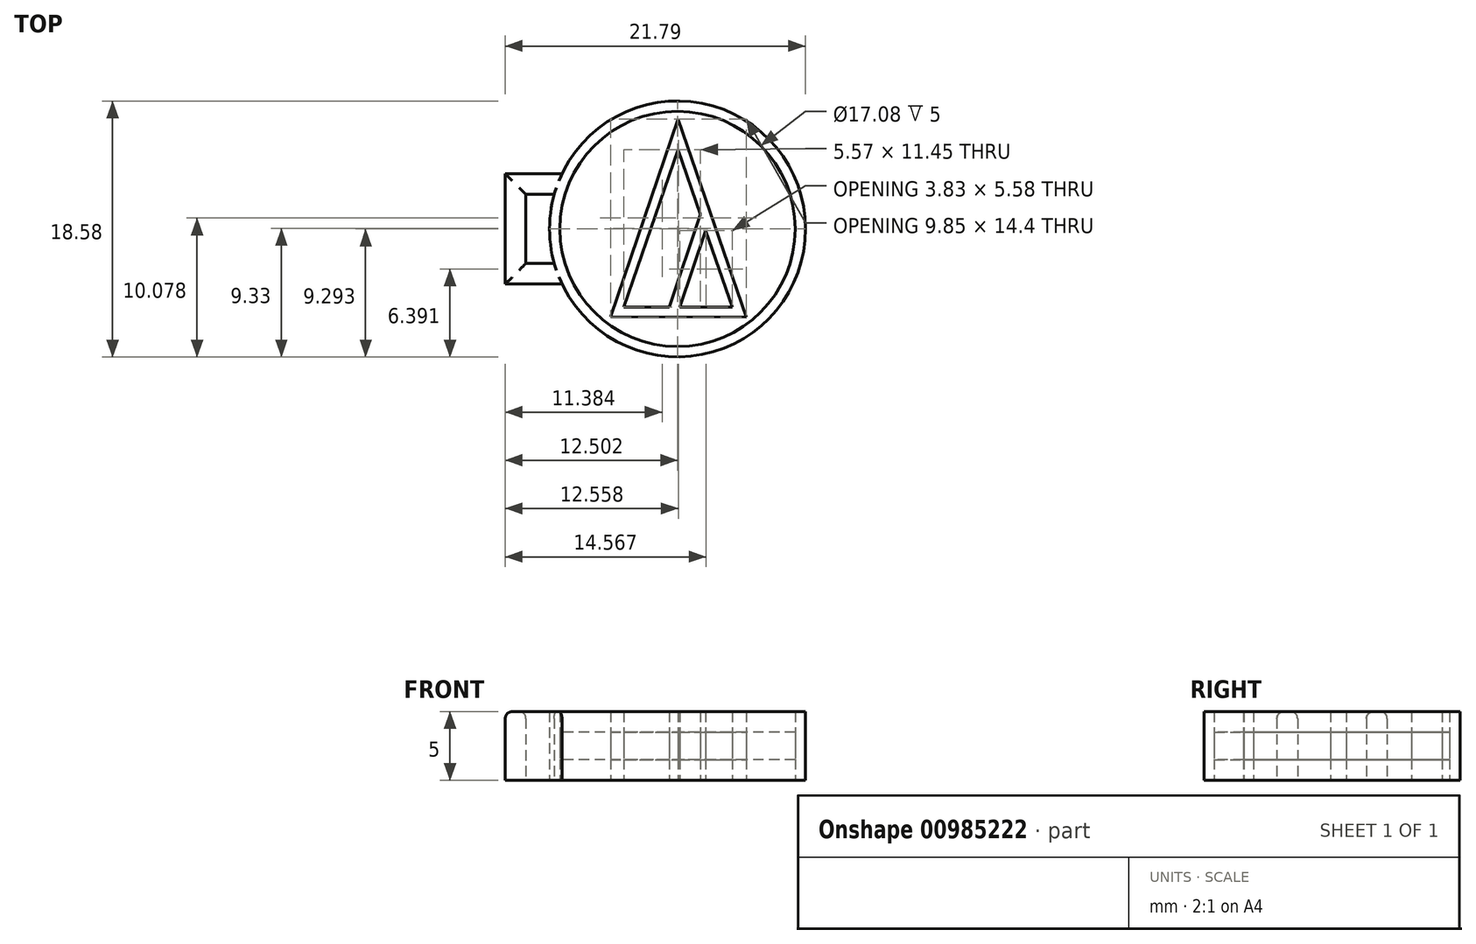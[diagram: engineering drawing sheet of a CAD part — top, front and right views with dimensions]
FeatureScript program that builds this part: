
annotation { "Feature Type Name" : "Feature", "Feature Type Description" : "" }
export const myFeature = defineFeature(function(context is Context, id is Id, definition is map)
    precondition{}
    {
        {
            var Q0;
            Q0=qCreatedBy(makeId("Top.planeOp"),FACE);
            var sketch = newSketch(context, id + "F0", { "sketchPlane" : qUnion([Q0])});
            skCircle(sketch, "E0", {"center": v(10.24, 10.22) * mm, "radius": 9.29 * mm});
            skCircle(sketch, "E1", {"center": v(10.24, 10.22) * mm, "radius": 8.54 * mm});
            skLineSegment(sketch, "E2", {"start": v(5.38, 3.83) * mm, "end": v(10.29, 18.2) * mm});
            skLineSegment(sketch, "E3", {"start": v(10.29, 18.2) * mm, "end": v(15.22, 3.81) * mm});
            skLineSegment(sketch, "E4", {"start": v(15.22, 3.81) * mm, "end": v(5.38, 3.83) * mm});
            skLineSegment(sketch, "E5", {"start": v(10.4, 4.53) * mm, "end": v(14.22, 4.53) * mm});
            skLineSegment(sketch, "E6", {"start": v(9.65, 4.54) * mm, "end": v(6.34, 4.54) * mm});
            skLineSegment(sketch, "E7", {"start": v(6.34, 4.54) * mm, "end": v(10.29, 15.98) * mm});
            skLineSegment(sketch, "E8", {"start": v(10.29, 15.98) * mm, "end": v(11.9, 11.27) * mm});
            skLineSegment(sketch, "E9", {"start": v(11.9, 11.27) * mm, "end": v(9.65, 4.54) * mm});
            skLineSegment(sketch, "E10", {"start": v(10.4, 4.53) * mm, "end": v(12.28, 10.11) * mm});
            skLineSegment(sketch, "E11", {"start": v(12.28, 10.11) * mm, "end": v(14.22, 4.53) * mm});
            skLineSegment(sketch, "E12.bottom", {"start": v(22.74, 14.22) * mm, "end": v(-2.26, 14.22) * mm});
            skLineSegment(sketch, "E12.top", {"start": v(22.74, 6.22) * mm, "end": v(-2.26, 6.22) * mm});
            skLineSegment(sketch, "E12.left", {"start": v(22.74, 14.22) * mm, "end": v(22.74, 6.22) * mm});
            skLineSegment(sketch, "E12.right", {"start": v(-2.26, 14.22) * mm, "end": v(-2.26, 6.22) * mm});
            skLineSegment(sketch, "E13.bottom", {"start": v(21.24, 12.72) * mm, "end": v(-0.76, 12.72) * mm});
            skLineSegment(sketch, "E13.top", {"start": v(21.24, 7.72) * mm, "end": v(-0.76, 7.72) * mm});
            skLineSegment(sketch, "E13.left", {"start": v(21.24, 12.72) * mm, "end": v(21.24, 7.72) * mm});
            skLineSegment(sketch, "E13.right", {"start": v(-0.76, 12.72) * mm, "end": v(-0.76, 7.72) * mm});
            skSolve(sketch);
        }
        {
            var Q0;
            {var subQ0=sQuery(id+"F0.wireOp",EDGE,"E13.bottom");var subQ1=sQuery(id+"F0.wireOp",EDGE,"E1");var subQ2=makeQuery(id+"F0.imprint","INTERSECT",VERTEX,{"disambiguationData":[OD(1.0)],"derivedFrom":[subQ1,subQ0]});Q0=makeQuery(id+"F0.imprint","IMPRINT",FACE,{"disambiguationData":[TD([[makeQuery(id+"F0.imprint","IMPRINT",EDGE,{"disambiguationData":[TD([[subQ2,-1.0]])],"derivedFrom":subQ1}),1.0]])]});}
            var Q1;
            {var subQ0=sQuery(id+"F0.wireOp",EDGE,"E12.bottom");var subQ1=sQuery(id+"F0.wireOp",EDGE,"E1");var subQ2=makeQuery(id+"F0.imprint","INTERSECT",VERTEX,{"disambiguationData":[OD(1.0)],"derivedFrom":[subQ1,subQ0]});Q1=makeQuery(id+"F0.imprint","IMPRINT",FACE,{"disambiguationData":[TD([[makeQuery(id+"F0.imprint","IMPRINT",EDGE,{"disambiguationData":[TD([[subQ2,-1.0]])],"derivedFrom":subQ1}),1.0]])]});}
            var Q2;
            {var subQ0=sQuery(id+"F0.wireOp",EDGE,"E12.bottom");var subQ1=sQuery(id+"F0.wireOp",EDGE,"E1");var subQ2=makeQuery(id+"F0.imprint","INTERSECT",VERTEX,{"disambiguationData":[OD(0.0)],"derivedFrom":[subQ1,subQ0]});Q2=makeQuery(id+"F0.imprint","IMPRINT",FACE,{"disambiguationData":[TD([[makeQuery(id+"F0.imprint","IMPRINT",EDGE,{"disambiguationData":[TD([[subQ2,-1.0]])],"derivedFrom":subQ1}),1.0]])]});}
            var Q3;
            {var subQ0=sQuery(id+"F0.wireOp",EDGE,"E12.bottom");var subQ1=sQuery(id+"F0.wireOp",EDGE,"E1");var subQ2=makeQuery(id+"F0.imprint","INTERSECT",VERTEX,{"disambiguationData":[OD(0.0)],"derivedFrom":[subQ1,subQ0]});Q3=makeQuery(id+"F0.imprint","IMPRINT",FACE,{"disambiguationData":[TD([[makeQuery(id+"F0.imprint","IMPRINT",EDGE,{"disambiguationData":[TD([[subQ2,1.0]])],"derivedFrom":subQ1}),1.0]])]});}
            var Q4;
            {var subQ0=sQuery(id+"F0.wireOp",EDGE,"E13.bottom");var subQ1=sQuery(id+"F0.wireOp",EDGE,"E1");var subQ2=makeQuery(id+"F0.imprint","INTERSECT",VERTEX,{"disambiguationData":[OD(0.0)],"derivedFrom":[subQ1,subQ0]});Q4=makeQuery(id+"F0.imprint","IMPRINT",FACE,{"disambiguationData":[TD([[makeQuery(id+"F0.imprint","IMPRINT",EDGE,{"disambiguationData":[TD([[subQ2,1.0]])],"derivedFrom":subQ1}),1.0]])]});}
            var Q5;
            {var subQ0=sQuery(id+"F0.wireOp",EDGE,"E12.top");var subQ1=sQuery(id+"F0.wireOp",EDGE,"E1");var subQ2=makeQuery(id+"F0.imprint","INTERSECT",VERTEX,{"disambiguationData":[OD(1.0)],"derivedFrom":[subQ1,subQ0]});Q5=makeQuery(id+"F0.imprint","IMPRINT",FACE,{"disambiguationData":[TD([[makeQuery(id+"F0.imprint","IMPRINT",EDGE,{"disambiguationData":[TD([[subQ2,-1.0]])],"derivedFrom":subQ1}),1.0]])]});}
            var Q6;
            {var subQ0=sQuery(id+"F0.wireOp",EDGE,"E4");Q6=makeQuery(id+"F0.imprint","IMPRINT",FACE,{"disambiguationData":[TD([[makeQuery(id+"F0.imprint","IMPRINT",EDGE,{"derivedFrom":subQ0}),1.0]])]});}
            var Q7;
            {var subQ0=sQuery(id+"F0.wireOp",EDGE,"E5");Q7=makeQuery(id+"F0.imprint","IMPRINT",FACE,{"disambiguationData":[TD([[makeQuery(id+"F0.imprint","IMPRINT",EDGE,{"derivedFrom":subQ0}),1.0]])]});}
            var Q8;
            {var subQ0=sQuery(id+"F0.wireOp",EDGE,"E12.top");var subQ1=sQuery(id+"F0.wireOp",EDGE,"E10");var subQ2=makeQuery(id+"F0.imprint","INTERSECT",VERTEX,{"derivedFrom":[subQ1,subQ0]});Q8=makeQuery(id+"F0.imprint","IMPRINT",FACE,{"disambiguationData":[TD([[makeQuery(id+"F0.imprint","IMPRINT",EDGE,{"disambiguationData":[TD([[subQ2,-1.0]])],"derivedFrom":subQ1}),-1.0]])]});}
            var Q9;
            {var subQ0=sQuery(id+"F0.wireOp",EDGE,"E11");var subQ1=sQuery(id+"F0.wireOp",EDGE,"E10");var subQ2=makeQuery(id+"F0.imprint","INTERSECT",VERTEX,{"derivedFrom":[subQ1,subQ0]});Q9=makeQuery(id+"F0.imprint","IMPRINT",FACE,{"disambiguationData":[TD([[makeQuery(id+"F0.imprint","IMPRINT",EDGE,{"disambiguationData":[TD([[subQ2,1.0]])],"derivedFrom":subQ1}),-1.0]])]});}
            var Q10;
            {var subQ1=sQuery(id+"F0.wireOp",EDGE,"E7");var subQ5=sQuery(id+"F0.wireOp",EDGE,"E13.top");var subQ6=makeQuery(id+"F0.imprint","INTERSECT",VERTEX,{"derivedFrom":[subQ1,subQ5]});Q10=makeQuery(id+"F0.imprint","IMPRINT",FACE,{"disambiguationData":[TD([[makeQuery(id+"F0.imprint","IMPRINT",EDGE,{"disambiguationData":[TD([[subQ6,-1.0]])],"derivedFrom":subQ1}),-1.0]])]});}
            var Q11;
            {var subQ0=sQuery(id+"F0.wireOp",EDGE,"E12.top");var subQ1=sQuery(id+"F0.wireOp",EDGE,"E7");var subQ2=makeQuery(id+"F0.imprint","INTERSECT",VERTEX,{"derivedFrom":[subQ1,subQ0]});Q11=makeQuery(id+"F0.imprint","IMPRINT",FACE,{"disambiguationData":[TD([[makeQuery(id+"F0.imprint","IMPRINT",EDGE,{"disambiguationData":[TD([[subQ2,-1.0]])],"derivedFrom":subQ1}),-1.0]])]});}
            var Q12;
            {var subQ0=sQuery(id+"F0.wireOp",EDGE,"E6");Q12=makeQuery(id+"F0.imprint","IMPRINT",FACE,{"disambiguationData":[TD([[makeQuery(id+"F0.imprint","IMPRINT",EDGE,{"derivedFrom":subQ0}),-1.0]])]});}
            var Q13;
            {var subQ0=sQuery(id+"F0.wireOp",EDGE,"E13.top");var subQ1=sQuery(id+"F0.wireOp",EDGE,"E1");var subQ2=makeQuery(id+"F0.imprint","INTERSECT",VERTEX,{"disambiguationData":[OD(0.0)],"derivedFrom":[subQ1,subQ0]});Q13=makeQuery(id+"F0.imprint","IMPRINT",FACE,{"disambiguationData":[TD([[makeQuery(id+"F0.imprint","IMPRINT",EDGE,{"disambiguationData":[TD([[subQ2,-1.0]])],"derivedFrom":subQ1}),1.0]])]});}
            var Q14;
            {var subQ0=sQuery(id+"F0.wireOp",EDGE,"E13.bottom");var subQ1=sQuery(id+"F0.wireOp",EDGE,"E7");var subQ2=makeQuery(id+"F0.imprint","INTERSECT",VERTEX,{"derivedFrom":[subQ1,subQ0]});Q14=makeQuery(id+"F0.imprint","IMPRINT",FACE,{"disambiguationData":[TD([[makeQuery(id+"F0.imprint","IMPRINT",EDGE,{"disambiguationData":[TD([[subQ2,-1.0]])],"derivedFrom":subQ1}),-1.0]])]});}
            var Q15;
            {var subQ0=sQuery(id+"F0.wireOp",EDGE,"E8");var subQ1=sQuery(id+"F0.wireOp",EDGE,"E7");var subQ2=makeQuery(id+"F0.imprint","INTERSECT",VERTEX,{"derivedFrom":[subQ1,subQ0]});Q15=makeQuery(id+"F0.imprint","IMPRINT",FACE,{"disambiguationData":[TD([[makeQuery(id+"F0.imprint","IMPRINT",EDGE,{"disambiguationData":[TD([[subQ2,1.0]])],"derivedFrom":subQ1}),-1.0]])]});}
            extrude(context, id + "F1", {"entities" : qUnion([Q0, Q1, Q2, Q3, Q4, Q5, Q6, Q7, Q8, Q9, Q10, Q11, Q12, Q13, Q14, Q15]), "endBound" : BoundingType.SYMMETRIC, "depth" : 2 * mm, "offsetDistance" : 25 * mm});
        }
        {
            var Q0;
            {var subQ0=sQuery(id+"F0.wireOp",EDGE,"E12.bottom");var subQ1=sQuery(id+"F0.wireOp",EDGE,"E0");var subQ2=makeQuery(id+"F0.imprint","INTERSECT",VERTEX,{"disambiguationData":[OD(0.0)],"derivedFrom":[subQ1,subQ0]});Q0=makeQuery(id+"F0.imprint","IMPRINT",FACE,{"disambiguationData":[TD([[makeQuery(id+"F0.imprint","IMPRINT",EDGE,{"disambiguationData":[TD([[subQ2,-1.0]])],"derivedFrom":subQ1}),1.0]])]});}
            var Q1;
            {var subQ6=sQuery(id+"F0.wireOp",EDGE,"E3");var subQ7=sQuery(id+"F0.wireOp",EDGE,"E2");var subQ8=makeQuery(id+"F0.imprint","INTERSECT",VERTEX,{"derivedFrom":[subQ7,subQ6]});Q1=makeQuery(id+"F0.imprint","IMPRINT",FACE,{"disambiguationData":[TD([[makeQuery(id+"F0.imprint","IMPRINT",EDGE,{"disambiguationData":[TD([[subQ8,1.0]])],"derivedFrom":subQ7}),-1.0]])]});}
            var Q2;
            {var subQ0=sQuery(id+"F0.wireOp",EDGE,"E12.bottom");var subQ1=sQuery(id+"F0.wireOp",EDGE,"E3");var subQ2=makeQuery(id+"F0.imprint","INTERSECT",VERTEX,{"derivedFrom":[subQ1,subQ0]});Q2=makeQuery(id+"F0.imprint","IMPRINT",FACE,{"disambiguationData":[TD([[makeQuery(id+"F0.imprint","IMPRINT",EDGE,{"disambiguationData":[TD([[subQ2,-1.0]])],"derivedFrom":subQ1}),-1.0]])]});}
            var Q3;
            {var subQ0=sQuery(id+"F0.wireOp",EDGE,"E13.bottom");var subQ1=sQuery(id+"F0.wireOp",EDGE,"E2");var subQ2=makeQuery(id+"F0.imprint","INTERSECT",VERTEX,{"derivedFrom":[subQ1,subQ0]});Q3=makeQuery(id+"F0.imprint","IMPRINT",FACE,{"disambiguationData":[TD([[makeQuery(id+"F0.imprint","IMPRINT",EDGE,{"disambiguationData":[TD([[subQ2,-1.0]])],"derivedFrom":subQ1}),-1.0]])]});}
            var Q4;
            {var subQ0=sQuery(id+"F0.wireOp",EDGE,"E13.top");var subQ1=sQuery(id+"F0.wireOp",EDGE,"E2");var subQ2=makeQuery(id+"F0.imprint","INTERSECT",VERTEX,{"derivedFrom":[subQ1,subQ0]});Q4=makeQuery(id+"F0.imprint","IMPRINT",FACE,{"disambiguationData":[TD([[makeQuery(id+"F0.imprint","IMPRINT",EDGE,{"disambiguationData":[TD([[subQ2,-1.0]])],"derivedFrom":subQ1}),-1.0]])]});}
            var Q5;
            {var subQ9=sQuery(id+"F0.wireOp",EDGE,"E13.bottom");var subQ11=sQuery(id+"F0.wireOp",EDGE,"E3");var subQ14=makeQuery(id+"F0.imprint","INTERSECT",VERTEX,{"derivedFrom":[subQ11,subQ9]});Q5=makeQuery(id+"F0.imprint","IMPRINT",FACE,{"disambiguationData":[TD([[makeQuery(id+"F0.imprint","IMPRINT",EDGE,{"disambiguationData":[TD([[subQ14,-1.0]])],"derivedFrom":subQ11}),-1.0]])]});}
            var Q6;
            {var subQ0=sQuery(id+"F0.wireOp",EDGE,"E13.top");var subQ1=sQuery(id+"F0.wireOp",EDGE,"E3");var subQ2=makeQuery(id+"F0.imprint","INTERSECT",VERTEX,{"derivedFrom":[subQ1,subQ0]});Q6=makeQuery(id+"F0.imprint","IMPRINT",FACE,{"disambiguationData":[TD([[makeQuery(id+"F0.imprint","IMPRINT",EDGE,{"disambiguationData":[TD([[subQ2,-1.0]])],"derivedFrom":subQ1}),-1.0]])]});}
            var Q7;
            {var subQ11=sQuery(id+"F0.wireOp",EDGE,"E4");Q7=makeQuery(id+"F0.imprint","IMPRINT",FACE,{"disambiguationData":[TD([[makeQuery(id+"F0.imprint","IMPRINT",EDGE,{"derivedFrom":subQ11}),-1.0]])]});}
            var Q8;
            {var subQ0=sQuery(id+"F0.wireOp",EDGE,"E13.top");var subQ1=sQuery(id+"F0.wireOp",EDGE,"E9");var subQ2=makeQuery(id+"F0.imprint","INTERSECT",VERTEX,{"derivedFrom":[subQ1,subQ0]});Q8=makeQuery(id+"F0.imprint","IMPRINT",FACE,{"disambiguationData":[TD([[makeQuery(id+"F0.imprint","IMPRINT",EDGE,{"disambiguationData":[TD([[subQ2,-1.0]])],"derivedFrom":subQ1}),1.0]])]});}
            var Q9;
            {var subQ0=sQuery(id+"F0.wireOp",EDGE,"E12.top");var subQ1=sQuery(id+"F0.wireOp",EDGE,"E2");var subQ2=makeQuery(id+"F0.imprint","INTERSECT",VERTEX,{"derivedFrom":[subQ1,subQ0]});Q9=makeQuery(id+"F0.imprint","IMPRINT",FACE,{"disambiguationData":[TD([[makeQuery(id+"F0.imprint","IMPRINT",EDGE,{"disambiguationData":[TD([[subQ2,-1.0]])],"derivedFrom":subQ1}),-1.0]])]});}
            var Q10;
            {var subQ0=sQuery(id+"F0.wireOp",EDGE,"E13.bottom");var subQ1=sQuery(id+"F0.wireOp",EDGE,"E0");var subQ2=makeQuery(id+"F0.imprint","INTERSECT",VERTEX,{"disambiguationData":[OD(1.0)],"derivedFrom":[subQ1,subQ0]});Q10=makeQuery(id+"F0.imprint","IMPRINT",FACE,{"disambiguationData":[TD([[makeQuery(id+"F0.imprint","IMPRINT",EDGE,{"disambiguationData":[TD([[subQ2,-1.0]])],"derivedFrom":subQ1}),1.0]])]});}
            var Q11;
            {var subQ0=sQuery(id+"F0.wireOp",EDGE,"E12.bottom");var subQ1=sQuery(id+"F0.wireOp",EDGE,"E0");var subQ2=makeQuery(id+"F0.imprint","INTERSECT",VERTEX,{"disambiguationData":[OD(1.0)],"derivedFrom":[subQ1,subQ0]});Q11=makeQuery(id+"F0.imprint","IMPRINT",FACE,{"disambiguationData":[TD([[makeQuery(id+"F0.imprint","IMPRINT",EDGE,{"disambiguationData":[TD([[subQ2,-1.0]])],"derivedFrom":subQ1}),1.0]])]});}
            var Q12;
            {var subQ0=sQuery(id+"F0.wireOp",EDGE,"E12.top");var subQ1=sQuery(id+"F0.wireOp",EDGE,"E0");var subQ2=makeQuery(id+"F0.imprint","INTERSECT",VERTEX,{"disambiguationData":[OD(0.0)],"derivedFrom":[subQ1,subQ0]});Q12=makeQuery(id+"F0.imprint","IMPRINT",FACE,{"disambiguationData":[TD([[makeQuery(id+"F0.imprint","IMPRINT",EDGE,{"disambiguationData":[TD([[subQ2,1.0]])],"derivedFrom":subQ1}),1.0]])]});}
            var Q13;
            {var subQ0=sQuery(id+"F0.wireOp",EDGE,"E12.top");var subQ1=sQuery(id+"F0.wireOp",EDGE,"E0");var subQ2=makeQuery(id+"F0.imprint","INTERSECT",VERTEX,{"disambiguationData":[OD(0.0)],"derivedFrom":[subQ1,subQ0]});Q13=makeQuery(id+"F0.imprint","IMPRINT",FACE,{"disambiguationData":[TD([[makeQuery(id+"F0.imprint","IMPRINT",EDGE,{"disambiguationData":[TD([[subQ2,-1.0]])],"derivedFrom":subQ1}),1.0]])]});}
            var Q14;
            {var subQ0=sQuery(id+"F0.wireOp",EDGE,"E12.top");var subQ1=sQuery(id+"F0.wireOp",EDGE,"E0");var subQ2=makeQuery(id+"F0.imprint","INTERSECT",VERTEX,{"disambiguationData":[OD(1.0)],"derivedFrom":[subQ1,subQ0]});Q14=makeQuery(id+"F0.imprint","IMPRINT",FACE,{"disambiguationData":[TD([[makeQuery(id+"F0.imprint","IMPRINT",EDGE,{"disambiguationData":[TD([[subQ2,-1.0]])],"derivedFrom":subQ1}),1.0]])]});}
            var Q15;
            {var subQ0=sQuery(id+"F0.wireOp",EDGE,"E13.bottom");var subQ1=sQuery(id+"F0.wireOp",EDGE,"E0");var subQ2=makeQuery(id+"F0.imprint","INTERSECT",VERTEX,{"disambiguationData":[OD(0.0)],"derivedFrom":[subQ1,subQ0]});Q15=makeQuery(id+"F0.imprint","IMPRINT",FACE,{"disambiguationData":[TD([[makeQuery(id+"F0.imprint","IMPRINT",EDGE,{"disambiguationData":[TD([[subQ2,1.0]])],"derivedFrom":subQ1}),1.0]])]});}
            var Q16;
            {var subQ0=sQuery(id+"F0.wireOp",EDGE,"E12.bottom");var subQ1=sQuery(id+"F0.wireOp",EDGE,"E0");var subQ2=makeQuery(id+"F0.imprint","INTERSECT",VERTEX,{"disambiguationData":[OD(0.0)],"derivedFrom":[subQ1,subQ0]});Q16=makeQuery(id+"F0.imprint","IMPRINT",FACE,{"disambiguationData":[TD([[makeQuery(id+"F0.imprint","IMPRINT",EDGE,{"disambiguationData":[TD([[subQ2,1.0]])],"derivedFrom":subQ1}),1.0]])]});}
            var Q17;
            {var subQ0=sQuery(id+"F0.wireOp",EDGE,"E12.right");Q17=makeQuery(id+"F0.imprint","IMPRINT",FACE,{"disambiguationData":[TD([[makeQuery(id+"F0.imprint","IMPRINT",EDGE,{"derivedFrom":subQ0}),1.0]])]});}
            extrude(context, id + "F2", {"entities" : qUnion([Q0, Q1, Q2, Q3, Q4, Q5, Q6, Q7, Q8, Q9, Q10, Q11, Q12, Q13, Q14, Q15, Q16, Q17]), "endBound" : BoundingType.SYMMETRIC, "depth" : 5 * mm, "offsetDistance" : 25 * mm});
        }
        {
            var Q0;
            Q0=makeQuery(id+"F2.opExtrude","CAP_EDGE",EDGE,{"disambiguationData":[OSD([sQuery(id+"F0.wireOp",EDGE,"E13.bottom")])],"isStart":false});
            var Q1;
            Q1=makeQuery(id+"F2.opExtrude","CAP_EDGE",EDGE,{"disambiguationData":[OSD([sQuery(id+"F0.wireOp",EDGE,"E13.right")])],"isStart":false});
            var Q2;
            Q2=makeQuery(id+"F2.opExtrude","CAP_EDGE",EDGE,{"disambiguationData":[OSD([sQuery(id+"F0.wireOp",EDGE,"E13.top")])],"isStart":false});
            var Q3;
            Q3=makeQuery(id+"F2.opExtrude","CAP_EDGE",EDGE,{"disambiguationData":[OSD([sQuery(id+"F0.wireOp",EDGE,"E12.top")])],"isStart":false});
            var Q4;
            Q4=makeQuery(id+"F2.opExtrude","CAP_EDGE",EDGE,{"disambiguationData":[OSD([sQuery(id+"F0.wireOp",EDGE,"E12.right")])],"isStart":false});
            var Q5;
            Q5=makeQuery(id+"F2.opExtrude","CAP_EDGE",EDGE,{"disambiguationData":[OSD([sQuery(id+"F0.wireOp",EDGE,"E12.bottom")])],"isStart":false});
            fillet(context, id + "F3", {"entities" : qUnion([Q0, Q1, Q2, Q3, Q4, Q5]), "radius" : 0.5 * mm, "tangentPropagation" : true, "allowEdgeOverflow" : false});
        }
    });
